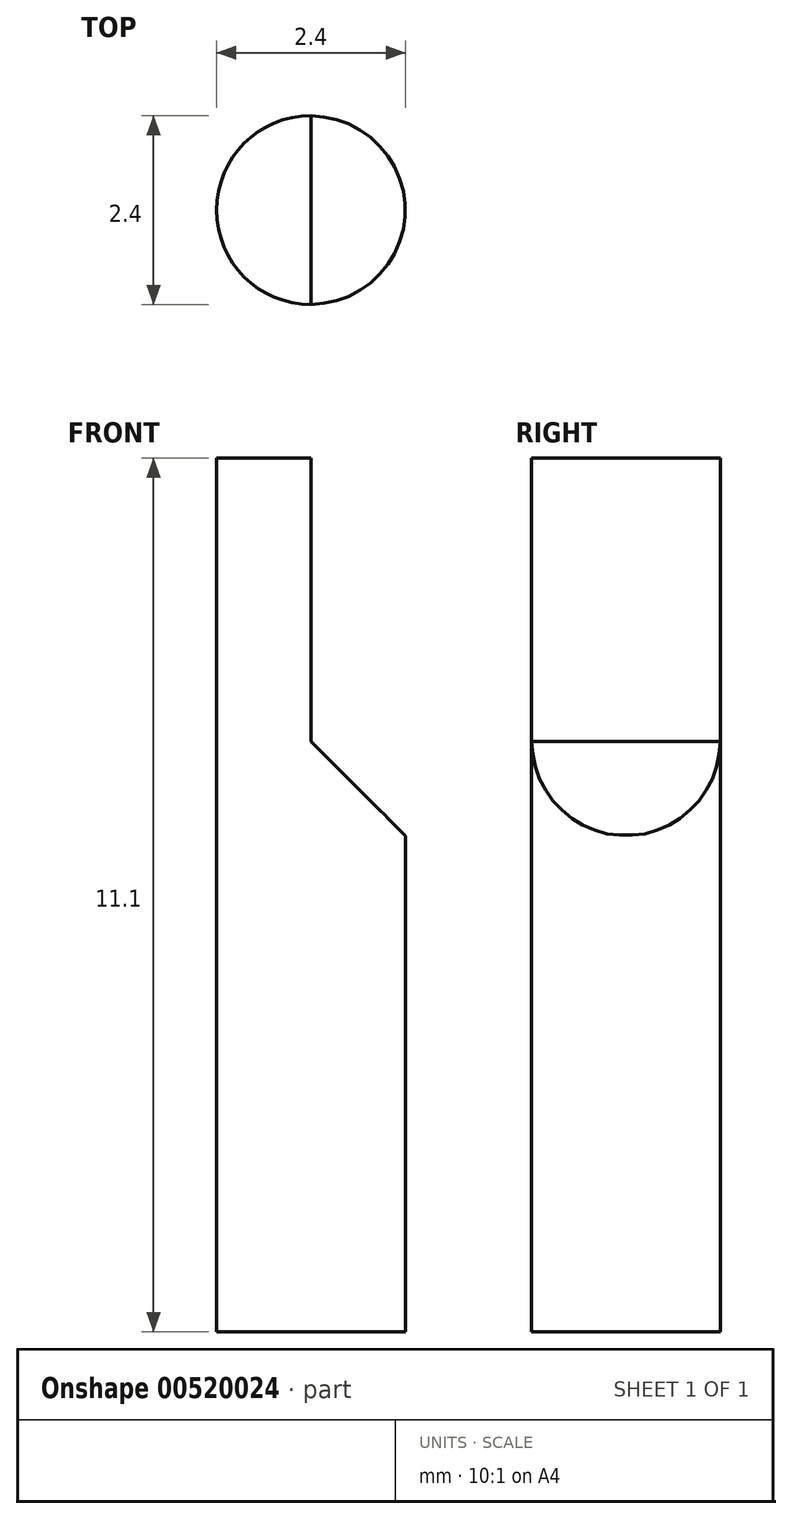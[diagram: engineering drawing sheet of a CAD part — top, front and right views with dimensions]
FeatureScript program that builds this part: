
annotation { "Feature Type Name" : "Feature", "Feature Type Description" : "" }
export const myFeature = defineFeature(function(context is Context, id is Id, definition is map)
    precondition{}
    {
        {
            var Q0;
            Q0=qCreatedBy(makeId("Top.planeOp"),FACE);
            var sketch = newSketch(context, id + "F0", { "sketchPlane" : qUnion([Q0])});
            skCircle(sketch, "E0", {"center": v(0, 0) * mm, "radius": 0.4 * mm});
            skSolve(sketch);
        }
        {
            var Q0;
            Q0=makeQuery(id+"F0.imprint","IMPRINT",FACE,{"disambiguationData":[TD([[makeQuery(id+"F0.imprint","IMPRINT",EDGE,{"derivedFrom":sQuery(id+"F0.wireOp",EDGE,"E0")}),1.0]])]});
            extrude(context, id + "F1", {"entities" : qUnion([Q0]), "depth" : 3.7 * mm});
        }
        {
            var Q0;
            Q0=makeQuery(id+"F1.opExtrude","SWEPT_BODY",BODY,{"disambiguationData":[OSD([sQuery(id+"F0.wireOp",EDGE,"E0")])]});
            transform(context, id + "F2", {"entities" : qUnion([Q0]), "transformType" : TransformType.TRANSLATION_3D, "dx" : 0 * mm, "dy" : 0 * mm, "dz" : 0 * mm, "makeCopy" : true});
        }
        {
            var Q0;
            Q0=qCreatedBy(makeId("Front.planeOp"),FACE);
            var sketch = newSketch(context, id + "F3", { "sketchPlane" : qUnion([Q0])});
            skLineSegment(sketch, "E1", {"start": v(0, 0) * mm, "end": v(0, 3.7) * mm, "construction": true});
            skLineSegment(sketch, "E2", {"start": v(0, 3.7) * mm, "end": v(0, 2.5) * mm});
            skLineSegment(sketch, "E3", {"start": v(0, 2.5) * mm, "end": v(0.4, 2.1) * mm});
            skLineSegment(sketch, "E4", {"start": v(0.4, 2.1) * mm, "end": v(0.4, 3.7) * mm});
            skLineSegment(sketch, "E5", {"start": v(0.4, 3.7) * mm, "end": v(0, 3.7) * mm});
            skSolve(sketch);
        }
        {
            var Q0;
            Q0=makeQuery(id+"F3.imprint","IMPRINT",FACE,{"disambiguationData":[TD([[makeQuery(id+"F3.imprint","IMPRINT",EDGE,{"derivedFrom":sQuery(id+"F3.wireOp",EDGE,"E2")}),1.0]])]});
            extrude(context, id + "F4", {"entities" : qUnion([Q0]), "operationType" : NewBodyOperationType.REMOVE, "endBound" : BoundingType.SYMMETRIC, "oppositeDirection" : true, "depth" : 1 * mm});
        }
        {
            var Q0;
            Q0=makeQuery(id+"F1.opExtrude","SWEPT_BODY",BODY,{"disambiguationData":[OSD([sQuery(id+"F0.wireOp",EDGE,"E0")])]});
            var Q1;
            Q1=makeQuery(id+"F2.opPattern","COPY",BODY,{"derivedFrom":makeQuery(id+"F1.opExtrude","SWEPT_BODY",BODY,{"disambiguationData":[OSD([sQuery(id+"F0.wireOp",EDGE,"E0")])]}),"instanceName":"1"});
            var Q2;
            Q2=qCreatedBy(makeId("Origin.pointOp"),VERTEX);
            transform(context, id + "F5", {"entities" : qUnion([Q0, Q1]), "transformType" : TransformType.SCALE_UNIFORMLY, "scale" : 3, "makeCopy" : false, "scalePoint" : qUnion([Q2])});
        }
    });
